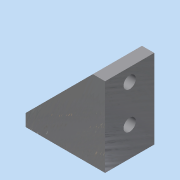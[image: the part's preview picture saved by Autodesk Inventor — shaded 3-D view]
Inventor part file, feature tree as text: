
AUTODESK INVENTOR PART (.ipt)
format: ipt  version: 2015 (Build 190159000, 159)  size: 142,848 bytes
history: native  units: in
note: dims shown in document units (in); Inventor stores cm internally (conversion verified against a paired STEP export)
features: sketch x6, extrude x5, hole x2
ambient origin geometry x8: Origin, YZ Plane, XZ Plane, XY Plane, X Axis, Y Axis, Z Axis, Center Point
bodies: Solid1 (feature_tree)
feature tree (13):
  extrude  "Extrusion1"  Depth=1.9685in
  sketch  "Sketch2"  dims[d2=0.7874in d3=0.0in d4=0.1969in]
  extrude  "Extrusion2"  Depth=0.1969in
  extrude  "Extrusion3"  Depth=0.1969in TaperAngle=0.0deg
  extrude  "Extrusion5"  Depth=0.5in
  hole  "Hole2"  [1 undecoded]
  hole  "Hole3"  [1 undecoded]
  extrude  "Extrusion6"  Depth=0.5906in
  sketch  "Sketch1"  dims[d0=1.9685in d1=1.9685in]
  sketch  "Sketch3"  dims[d5=0.1969in d6=0.2953in d7=0.0in]
  sketch  "Sketch5"  dims[d8=0.1969in d9=0.0in d12=0.5in]
  sketch  "Sketch6"  dims[d13=0.5in d14=0.0in d15=0.0in]
  sketch  "Sketch7"  dims[d28=0.3937in d29=0.3937in d30=0.5906in d31=0.4724in d32=0.1969in d33=0.75in d34=0.375in d35=0.25in d36=0.5635in d37=1.0in d38=0.8108in d39=0.5906in d40=0.3937in d41=0.3937in d42=0.4724in d43=0.1969in d44=0.75in d45=0.375in d46=0.25in d47=0.5635in d48=1.0in d49=0.8108in d50=1.0in d51=0.0in]
note: 2 required parameter values undecoded (feature->parameter linkage not recoverable at this tier; creation-order binding heuristic only, values carry confidence <= 0.55)
